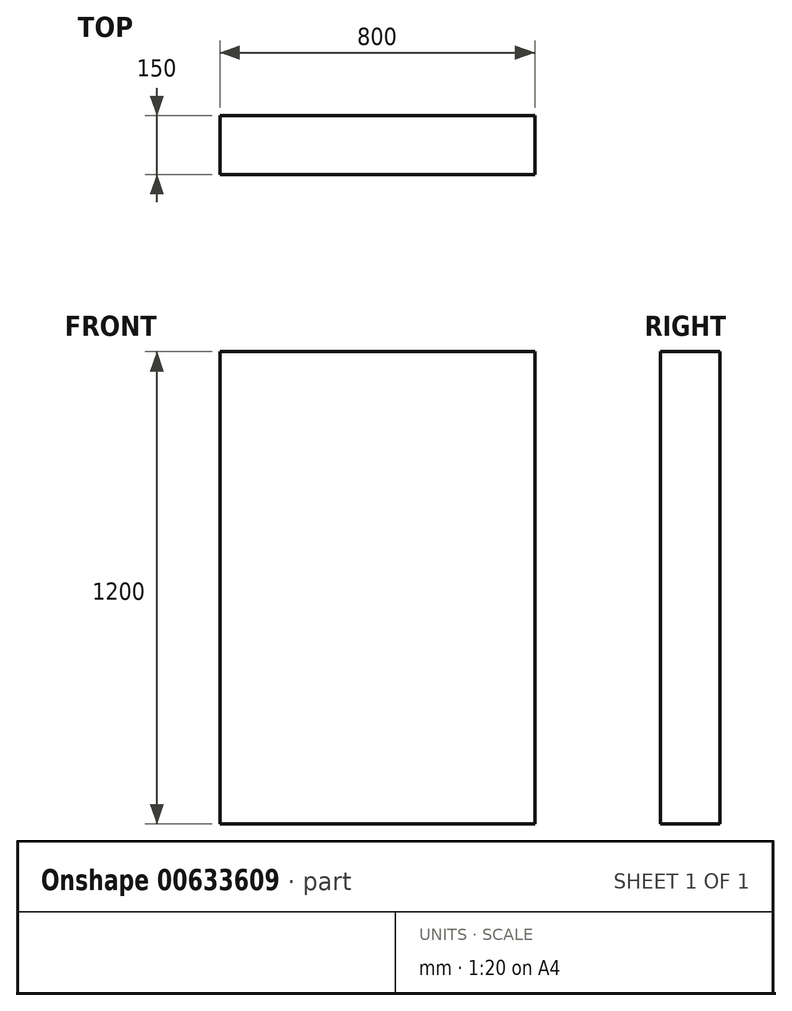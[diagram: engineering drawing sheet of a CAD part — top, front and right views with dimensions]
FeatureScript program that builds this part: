
annotation { "Feature Type Name" : "Feature", "Feature Type Description" : "" }
export const myFeature = defineFeature(function(context is Context, id is Id, definition is map)
    precondition{}
    {
        {
            var Q0;
            Q0=qCreatedBy(makeId("Front.planeOp"),FACE);
            var sketch = newSketch(context, id + "F0", { "sketchPlane" : qUnion([Q0])});
            skLineSegment(sketch, "E0.bottom", {"start": v(400, 600) * mm, "end": v(-400, 600) * mm});
            skLineSegment(sketch, "E0.top", {"start": v(400, -600) * mm, "end": v(-400, -600) * mm});
            skLineSegment(sketch, "E0.left", {"start": v(400, 600) * mm, "end": v(400, -600) * mm});
            skLineSegment(sketch, "E0.right", {"start": v(-400, 600) * mm, "end": v(-400, -600) * mm});
            skPoint(sketch, "E0.middle", {"position": v(0, 0) * mm});
            skSolve(sketch);
        }
        {
            var Q0;
            Q0=makeQuery(id+"F0.imprint","IMPRINT",FACE,{"disambiguationData":[TD([[makeQuery(id+"F0.imprint","IMPRINT",EDGE,{"derivedFrom":sQuery(id+"F0.wireOp",EDGE,"E0.bottom")}),1.0]])]});
            extrude(context, id + "F1", {"entities" : qUnion([Q0]), "depth" : 150 * mm, "offsetDistance" : 25.4 * mm});
        }
    });
